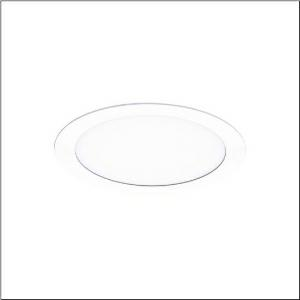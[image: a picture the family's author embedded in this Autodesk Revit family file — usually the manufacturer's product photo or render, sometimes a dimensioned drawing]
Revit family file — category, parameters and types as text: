
# Revit family: lunis_21_xl_51db16ef91c
name_source: partatom
category: Lighting Fixtures
units: mm (PartAtom-declared; Revit-internal decimal feet)

## family parameters
Cut with Voids When Loaded = No
Host = Face
Light Source = No
Part Type = Normal
Room Calculation Point = No
Round Connector Dimension = Use Diameter
Shared = No

## types (1)
- --- (1 x LED, 3300 lm, 25.4 W, 6500K)
    Apparent Load = 25 VA
    CIE Flux Codes = 50 80 96 100 100
    Color Rendering = 80
    Color Temperature = 6500K
    Default Elevation = 1800 mm
    Description = Lunis 21 XL, downlight, light control with lens, of PMMA, optical cover: cover panel, of PC, opal, light emission: direct distribution, LED rated luminous flux: 1.960lm, light colour: 830/840/865, with terminal, 5-pole, mains connection: 220..240V, AC/DC, 0/50..60Hz, housing, round, of diecast aluminium, traffic white (RAL 9016), diameter: 230mm, clamping range: 1..40mm, protection rating (complete): IP20, protection rating (on room side): IP54, insulation class (complete): insulation class II (safety insulation), certification: CE, impact resistance: IK03, packaging unit: 1 piece
    Height = 0 mm  [stored 0 ft]
    Lamp = 1 x LED
    Lamp Light Flux = 3300 lm
    Lamp Power = 25.4 W
    Lamp count = 1
    Length = 230 mm
    Luminous efficacy = 130 lm/W
    Manufacturer = Siteco
    ModVariant = No
    Model = 51DB16EF91C
    Mounting Place = Ceiling
    Mounting Type = Recessed
    Number of Poles = 1
    OnlyDefault = Yes
    Power Factor = 1
    Product Name = Lunis 21 XL
    Product group = downlight
    ProductGroupID = 401
    Protection Class = Protection class II
    Protection Degree = IP 20
    RLX_Detail_Level = 1
    RLX_Emergency_Light_Flux = 0 lm
    RLX_Emergency_Type = 0
    RLX_Emergency_Type_DB = No
    RlxData = <blob elided: 18729 chars, md5=20917dad>
    Socket = socket
    Standby Power = 0 W
    System Light Flux = 3300 lm
    System Power = 25 W
    Type Comments = individual setting: colour temperature 6500K, luminous flux: 100 % | (ON | ON | OFF | OFF) | 700 mA
    Type Image = l_1291153.jpg
    URL = http://relux.com
    VarID = @adj_036663
    Voltage = 0 V
    Weight = 0.00 kg
    Width = 0 mm  [stored 0 ft]

note: [stored X ft] marks values corroborated as IEEE doubles in the binary element streams (Revit-internal decimal feet)

## geometry (parser evidence)
native form markers: Blend x4, Sweep x8
no freeform markers — native parametric forms only
